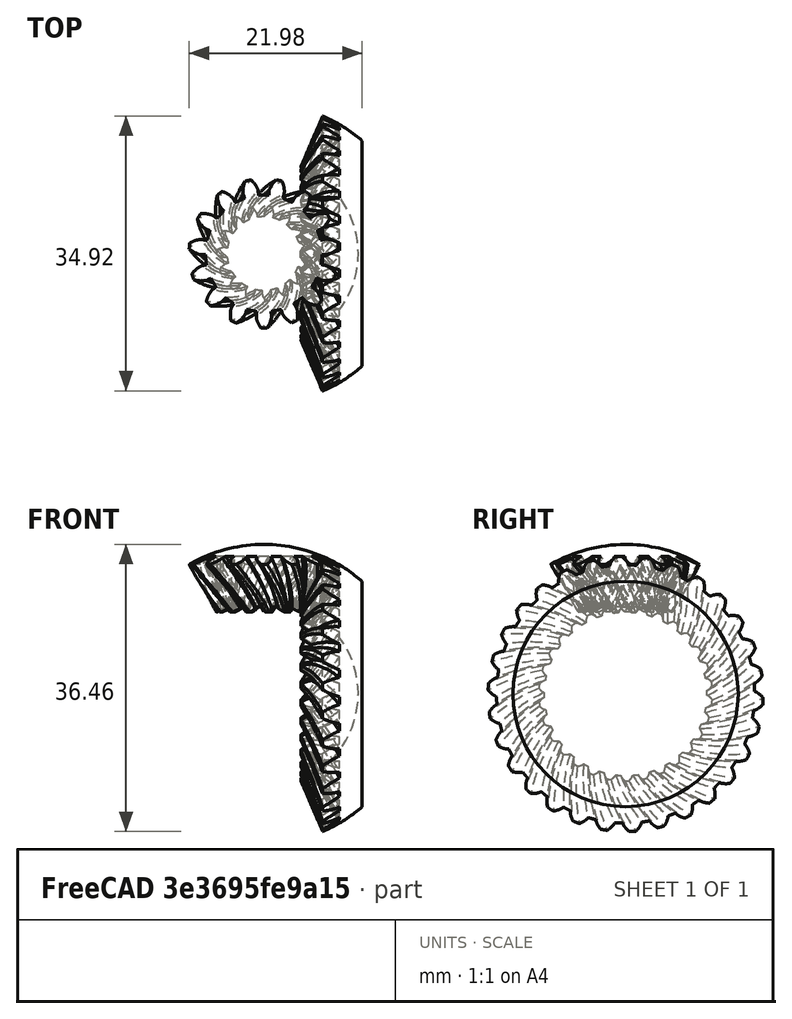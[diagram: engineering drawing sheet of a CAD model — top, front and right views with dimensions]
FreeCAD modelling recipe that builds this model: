
FCSTD DOCUMENT  (FreeCAD 0.19R21654 (Git))
Label: bevel_gear_animation
License: All rights reserved
LicenseURL: http://en.wikipedia.org/wiki/All_rights_reserved
objects: Part::Sphere×2, Part::FeaturePython×2, Part::MultiCommon×2, Part::Cut×1
note: 7 computed .brp shape members not serialized (recipe doc carries the construction recipe); baked Part::Feature solids carry a one-line shape summary decoded from their .brp

FEATURE [Part::Sphere] Sphere  label="Kugel"
  Angle1 = -90
  Angle2 = 90
  Angle3 = 360
  AttacherType = Attacher::AttachEngine3D
  Placement = pos=(0,0,0) rot=(0,0,1;1.5708rad)
  Radius = 12
FEATURE [Part::Sphere] Sphere001  label="Kugel001"
  Angle1 = -90
  Angle2 = 90
  Angle3 = 360
  AttacherType = Attacher::AttachEngine3D
  Placement = pos=(0,0,0) rot=(0,0,1;1.5708rad)
  Radius = 19
FEATURE [Part::Cut] Cut
  Base = -> Sphere001
  Tool = -> Sphere
FEATURE [Part::FeaturePython] BevelGear002  label="BevelGear001"  # WARN: FeaturePython — macro-defined, semantics opaque (R4)
  Placement = pos=(0,0,0) rot=(0,0,1;0.10472rad)
  backlash = 0
  beta = 20
  clearance = 0.1
  height = 10
  m = 1
  numpoints = 6
  pitch_angle = 26.5651
  pressure_angle = 20
  reset_origin = false
  teeth = 15
  expr: pitch_angle = atan(0.5)
FEATURE [Part::MultiCommon] Common001
  Shapes = -> [Cut,BevelGear002]
FEATURE [Part::FeaturePython] BevelGear  # WARN: FeaturePython — macro-defined, semantics opaque (R4)
  Placement = pos=(0,0,0) rot=(0,1,0;1.5708rad)
  backlash = 0
  beta = -20
  clearance = 0.1
  height = 10
  m = 1
  numpoints = 6
  pitch_angle = 63.4349
  pressure_angle = 20
  reset_origin = false
  teeth = 30
  expr: pitch_angle = 90° - atan(0.5)
FEATURE [Part::MultiCommon] Common
  Shapes = -> [Cut,BevelGear]
